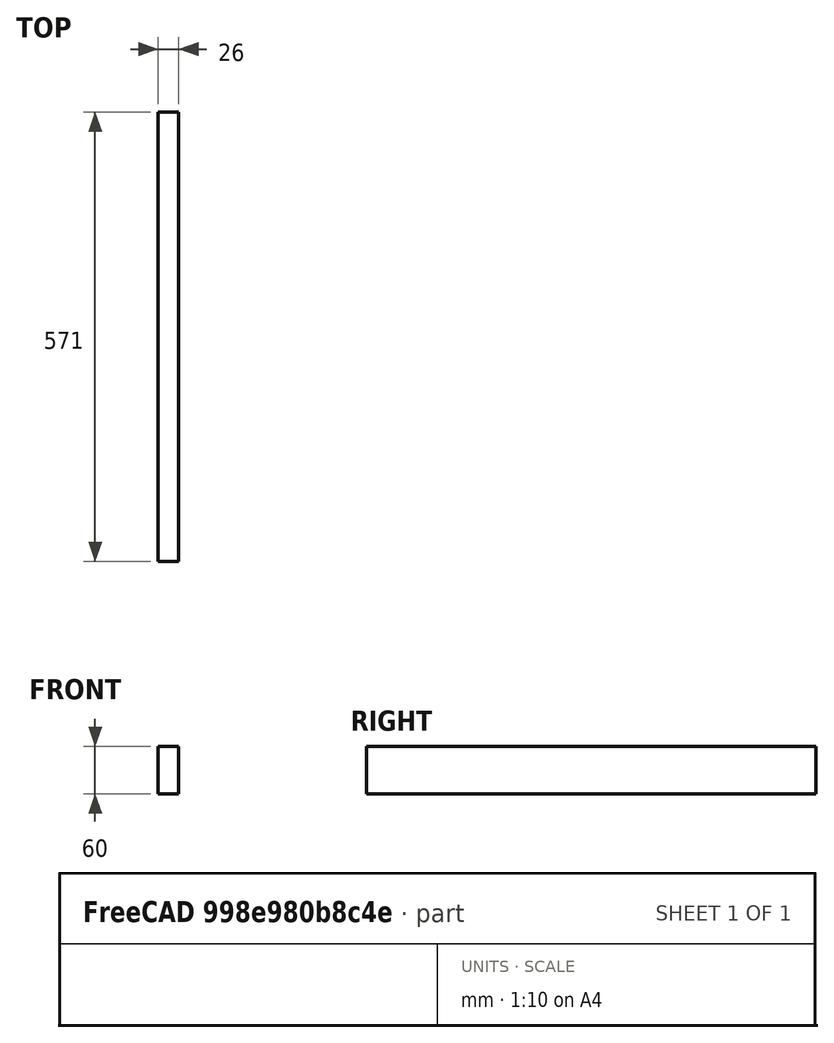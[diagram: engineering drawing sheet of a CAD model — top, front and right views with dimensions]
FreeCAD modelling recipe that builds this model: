
FCSTD DOCUMENT  (FreeCAD 0.20R29603 (Git))
Label: JoueStand
License: All rights reserved
LicenseURL: http://en.wikipedia.org/wiki/All_rights_reserved
objects: Drawing::FeatureViewPython×6, Drawing::FeatureViewPart×2, Part::Box×1, Drawing::FeaturePage×1
note: 1 computed .brp shape members not serialized (recipe doc carries the construction recipe); baked Part::Feature solids carry a one-line shape summary decoded from their .brp

FEATURE [Part::Box] Box  label="Cube"
  AttacherType = Attacher::AttachEngine3D
  Height = 60
  Length = 26
  Width = 571
FEATURE [Drawing::FeatureViewPart] Ortho  label="Ortho_0_0"
  Direction = (0,0,1)
  HiddenWidth = 0.15
  LineWidth = 0.35
  Rotation = 90
  Scale = 0.25
  ShowHiddenLines = false
  ShowSmoothLines = false
  Tolerance = 0.05
  ViewResult = <g id="Ortho_0_0"\n   transform="rotate(90,77.25,113.021) translate(77.25,113.021) scale(0.25,0.25)"\n  >\n<g   fill="none"\n   stroke="rgb(0, 0, 0)"\n   stroke-linecap="butt"\n   stroke-linejoin="miter"\n   stroke-width="1.400000"\n   transform="scale(1,-1)"\n  >\n<path id= "1" d=" M 0 0 L 0 570 " />\n<path id= "2" d=" M 0 0 L 5 0 " />\n<path id= "3" d=" M 0 570 L 31 570 " />\n<path id= "4" d=" M 31 26 L 31 570 " />\n<path d="M5 0 A26 26 0 0 1 31 26" /></g>\n</g>
  Visible = false
  X = 77.25
  Y = 113.021
FEATURE [Drawing::FeatureViewPart] Ortho001  label="Ortho_0_1"
  Direction = (1,0,0)
  HiddenWidth = 0.15
  LineWidth = 0.35
  Rotation = -90
  Scale = 0.25
  ShowHiddenLines = false
  ShowSmoothLines = false
  Tolerance = 0.05
  ViewResult = <g id="Ortho_0_1"\n   transform="rotate(-90,77.25,68.0417) translate(77.25,68.0417) scale(0.25,0.25)"\n  >\n<g   fill="none"\n   stroke="rgb(0, 0, 0)"\n   stroke-linecap="butt"\n   stroke-linejoin="miter"\n   stroke-width="1.400000"\n   transform="scale(1,-1)"\n  >\n<path id= "1" d=" M 60 0 L 0 0 " />\n<path id= "2" d=" M 60 -26 L 60 -570 " />\n<path d="M60,0 L60,-0.163483  L60,-0.651874  L60,-1.45903  L60,-2.57481  L60,-3.98517  L60,-5.67238  L60,-7.61522  L60,-9.78927  L60,-12.1672  L60,-14.719  L60,-17.4127  L60,-20.2145  L60,-23.0889  L60,-26 " /><path id= "4" d=" M 0 -570 L 60 -570 " />\n<path id= "5" d=" M 0 -26 L 0 -570 " />\n<path d="M0,0 L0,-0.163483  L0,-0.651874  L0,-1.45903  L0,-2.57481  L0,-3.98517  L0,-5.67238  L0,-7.61522  L0,-9.78927  L0,-12.1672  L0,-14.719  L0,-17.4127  L0,-20.2145  L0,-23.0889  L0,-26 " /><path id= "7" d=" M 60 -26 L 0 -26 " />\n</g>\n</g>
  Visible = false
  X = 77.25
  Y = 68.0417
FEATURE [Drawing::FeatureViewPython] dim001  # drawing view (typed FeaturePython)
  Rotation = 0
  ViewResult = <g> \n  <line x1="77.250000" y1="111.021000" x2="77.250000" y2="99.000000" style="stroke:rgb(0,0,255);stroke-width:0.30" />\n<line x1="219.750000" y1="111.021000" x2="219.750000" y2="99.000000" style="stroke:rgb(0,0,255);stroke-width:0.30" />\n<line x1="77.250000" y1="100.000000" x2="219.750000" y2="100.000000" style="stroke:rgb(0,0,255);stroke-width:0.30" /> \n  <polygon points="219.750000,100.000000 216.750000,99.000000 215.750000,100.000000 216.750000,101.000000" style="fill:rgb(0,0,255);stroke:rgb(0,0,255);stroke-width:0" /><polygon points="77.250000,100.000000 80.250000,101.000000 81.250000,100.000000 80.250000,99.000000" style="fill:rgb(0,0,255);stroke:rgb(0,0,255);stroke-width:0" /> \n  <text x="148.500000" y="98.000000" font-family="Verdana" font-size="3.6" fill="rgb(0,0,255)" text-anchor="middle" transform="rotate(0.000000 148.500000,98.000000)" >570</text> </g>
  Visible = true
  X = 0
  Y = 0
  arrowL1 = 3
  arrowL2 = 1
  arrowW = 2
  arrow_scheme = 0
  autoPlaceOffset = 2
  autoPlaceText = true
  click1_x = 135
  click1_y = 100
  click2_x = 135
  click2_y = 100
  comma_decimal_place = false
  dimension_line_overshoot = 1
  gap_datum_points = 2
  halfDimension_linear = false
  lineColor = rgb(0,0,255)
  strokeWidth = 0.3
  textFormat_linear = %(value)3.0f
  textRenderer_color = rgb(0,0,255)
  textRenderer_family = Verdana
  textRenderer_size = 3.6
  unit_custom_scale = 1
  unit_scheme = 0
FEATURE [Drawing::FeatureViewPython] dim002  # drawing view (typed FeaturePython)
  Rotation = 0
  ViewResult = <g> \n  <line x1="83.750000" y1="122.771000" x2="83.750000" y2="141.000000" style="stroke:rgb(0,0,255);stroke-width:0.30" />\n<line x1="219.750000" y1="122.771000" x2="219.750000" y2="141.000000" style="stroke:rgb(0,0,255);stroke-width:0.30" />\n<line x1="83.750000" y1="140.000000" x2="219.750000" y2="140.000000" style="stroke:rgb(0,0,255);stroke-width:0.30" /> \n  <polygon points="219.750000,140.000000 216.750000,139.000000 215.750000,140.000000 216.750000,141.000000" style="fill:rgb(0,0,255);stroke:rgb(0,0,255);stroke-width:0" /><polygon points="83.750000,140.000000 86.750000,141.000000 87.750000,140.000000 86.750000,139.000000" style="fill:rgb(0,0,255);stroke:rgb(0,0,255);stroke-width:0" /> \n  <text x="151.750000" y="138.000000" font-family="Verdana" font-size="3.6" fill="rgb(0,0,255)" text-anchor="middle" transform="rotate(0.000000 151.750000,138.000000)" >544</text> </g>
  Visible = true
  X = 0
  Y = 0
  arrowL1 = 3
  arrowL2 = 1
  arrowW = 2
  arrow_scheme = 0
  autoPlaceOffset = 2
  autoPlaceText = true
  click1_x = 155
  click1_y = 140
  click2_x = 155
  click2_y = 140
  comma_decimal_place = false
  dimension_line_overshoot = 1
  gap_datum_points = 2
  halfDimension_linear = false
  lineColor = rgb(0,0,255)
  strokeWidth = 0.3
  textFormat_linear = %(value)3.0f
  textRenderer_color = rgb(0,0,255)
  textRenderer_family = Verdana
  textRenderer_size = 3.6
  unit_custom_scale = 1
  unit_scheme = 0
FEATURE [Drawing::FeatureViewPython] dim003  # drawing view (typed FeaturePython)
  Rotation = 0
  ViewResult = <g> \n  <line x1="221.750000" y1="113.021000" x2="251.000000" y2="113.021000" style="stroke:rgb(0,0,255);stroke-width:0.30" />\n<line x1="221.750000" y1="120.771000" x2="251.000000" y2="120.771000" style="stroke:rgb(0,0,255);stroke-width:0.30" />\n<line x1="250.000000" y1="113.021000" x2="250.000000" y2="120.771000" style="stroke:rgb(0,0,255);stroke-width:0.30" /> \n  <polygon points="250.000000,120.771000 249.000000,123.771000 250.000000,124.771000 251.000000,123.771000" style="fill:rgb(0,0,255);stroke:rgb(0,0,255);stroke-width:0" /><polygon points="250.000000,113.021000 251.000000,110.021000 250.000000,109.021000 249.000000,110.021000" style="fill:rgb(0,0,255);stroke:rgb(0,0,255);stroke-width:0" /> \n  <text x="248.000000" y="116.896000" font-family="Verdana" font-size="3.6" fill="rgb(0,0,255)" text-anchor="middle" transform="rotate(-90.000000 248.000000,116.896000)" > 31</text> </g>
  Visible = true
  X = 0
  Y = 0
  arrowL1 = 3
  arrowL2 = 1
  arrowW = 2
  arrow_scheme = 0
  autoPlaceOffset = 2
  autoPlaceText = true
  click1_x = 250
  click1_y = 115
  click2_x = 250
  click2_y = 115
  comma_decimal_place = false
  dimension_line_overshoot = 1
  gap_datum_points = 2
  halfDimension_linear = false
  lineColor = rgb(0,0,255)
  strokeWidth = 0.3
  textFormat_linear = %(value)3.0f
  textRenderer_color = rgb(0,0,255)
  textRenderer_family = Verdana
  textRenderer_size = 3.6
  unit_custom_scale = 1
  unit_scheme = 0
FEATURE [Drawing::FeatureViewPython] dim004  # drawing view (typed FeaturePython)
  Rotation = 0
  ViewResult = <g> \n  <line x1="221.750000" y1="68.041700" x2="251.000000" y2="68.041700" style="stroke:rgb(0,0,255);stroke-width:0.30" />\n<line x1="221.750000" y1="53.041700" x2="251.000000" y2="53.041700" style="stroke:rgb(0,0,255);stroke-width:0.30" />\n<line x1="250.000000" y1="68.041700" x2="250.000000" y2="53.041700" style="stroke:rgb(0,0,255);stroke-width:0.30" /> \n  <polygon points="250.000000,53.041700 249.000000,56.041700 250.000000,57.041700 251.000000,56.041700" style="fill:rgb(0,0,255);stroke:rgb(0,0,255);stroke-width:0" /><polygon points="250.000000,68.041700 251.000000,65.041700 250.000000,64.041700 249.000000,65.041700" style="fill:rgb(0,0,255);stroke:rgb(0,0,255);stroke-width:0" /> \n  <text x="248.000000" y="60.541700" font-family="Verdana" font-size="3.6" fill="rgb(0,0,255)" text-anchor="middle" transform="rotate(-90.000000 248.000000,60.541700)" > 60</text> </g>
  Visible = true
  X = 0
  Y = 0
  arrowL1 = 3
  arrowL2 = 1
  arrowW = 2
  arrow_scheme = 0
  autoPlaceOffset = 2
  autoPlaceText = true
  click1_x = 250
  click1_y = 55
  click2_x = 250
  click2_y = 55
  comma_decimal_place = false
  dimension_line_overshoot = 1
  gap_datum_points = 2
  halfDimension_linear = false
  lineColor = rgb(0,0,255)
  strokeWidth = 0.3
  textFormat_linear = %(value)3.0f
  textRenderer_color = rgb(0,0,255)
  textRenderer_family = Verdana
  textRenderer_size = 3.6
  unit_custom_scale = 1
  unit_scheme = 0
FEATURE [Drawing::FeatureViewPython] rad001  # drawing view (typed FeaturePython)
  Rotation = 0
  ViewResult = <g>  <circle cx ="83.750000" cy ="114.271000" r="0.500000" stroke="none" fill="rgb(0,0,255)" /> \n<line x1="60.000000" y1="140.000000" x2="83.750000" y2="114.271000" style="stroke:rgb(0,0,255);stroke-width:0.30" />\n<polygon points="79.341164,119.047208 82.110813,117.521087 82.054294,116.108003 80.641210,116.164522" style="fill:rgb(0,0,255);stroke:rgb(0,0,255);stroke-width:0" />\n<line x1="60.000000" y1="140.000000" x2="40.000000" y2="140.000000" style="stroke:rgb(0,0,255);stroke-width:0.30" />\n<text x="50.000000" y="138.000000" font-family="Verdana" font-size="3.6" fill="rgb(0,0,255)" text-anchor="middle" transform="rotate(0.000000 50.000000,138.000000)" >R 26</text> </g>
  Visible = true
  X = 0
  Y = 0
  arrowL1 = 3
  arrowL2 = 1
  arrowW = 2
  arrow_scheme = 0
  autoPlaceOffset = 2
  autoPlaceText = true
  centerPointDia = 1
  click1_x = 60
  click1_y = 140
  click2_x = 40
  click2_y = 140
  click3_x = 40
  click3_y = 140
  comma_decimal_place = false
  lineColor = rgb(0,0,255)
  strokeWidth = 0.3
  textFormat_radial = R%(value)3.0f
  textRenderer_color = rgb(0,0,255)
  textRenderer_family = Verdana
  textRenderer_size = 3.6
  unit_custom_scale = 1
  unit_scheme = 0
FEATURE [Drawing::FeatureViewPython] dim005  # drawing view (typed FeaturePython)
  Rotation = 0
  ViewResult = <g> \n  <line x1="75.250000" y1="113.021000" x2="59.000000" y2="113.021000" style="stroke:rgb(0,0,255);stroke-width:0.30" />\n<line x1="75.250000" y1="114.271000" x2="59.000000" y2="114.271000" style="stroke:rgb(0,0,255);stroke-width:0.30" />\n<line x1="60.000000" y1="113.021000" x2="60.000000" y2="114.271000" style="stroke:rgb(0,0,255);stroke-width:0.30" /> \n  <polygon points="60.000000,114.271000 59.000000,117.271000 60.000000,118.271000 61.000000,117.271000" style="fill:rgb(0,0,255);stroke:rgb(0,0,255);stroke-width:0" /><polygon points="60.000000,113.021000 61.000000,110.021000 60.000000,109.021000 59.000000,110.021000" style="fill:rgb(0,0,255);stroke:rgb(0,0,255);stroke-width:0" /> \n  <text x="58.000000" y="113.646000" font-family="Verdana" font-size="3.6" fill="rgb(0,0,255)" text-anchor="middle" transform="rotate(-90.000000 58.000000,113.646000)" >  5</text> </g>
  Visible = true
  X = 0
  Y = 0
  arrowL1 = 3
  arrowL2 = 1
  arrowW = 2
  arrow_scheme = 0
  autoPlaceOffset = 2
  autoPlaceText = true
  click1_x = 60
  click1_y = 110
  click2_x = 60
  click2_y = 110
  comma_decimal_place = false
  dimension_line_overshoot = 1
  gap_datum_points = 2
  halfDimension_linear = false
  lineColor = rgb(0,0,255)
  strokeWidth = 0.3
  textFormat_linear = %(value)3.0f
  textRenderer_color = rgb(0,0,255)
  textRenderer_family = Verdana
  textRenderer_size = 3.6
  unit_custom_scale = 1
  unit_scheme = 0
FEATURE [Drawing::FeaturePage] Page
  EditableTexts = GB | Joue stand | 2 exemplaires | A4 | X / Y | 1/4 | PN | DN | DD/MM/YYYY | REV A
  Group = -> [Ortho,Ortho001,dim001,dim002,dim003,dim004,rad001,dim005]
  Template = <path>
note: 1 file-system path scrubbed to <path> (originals preserved in the JSON sidecar)
